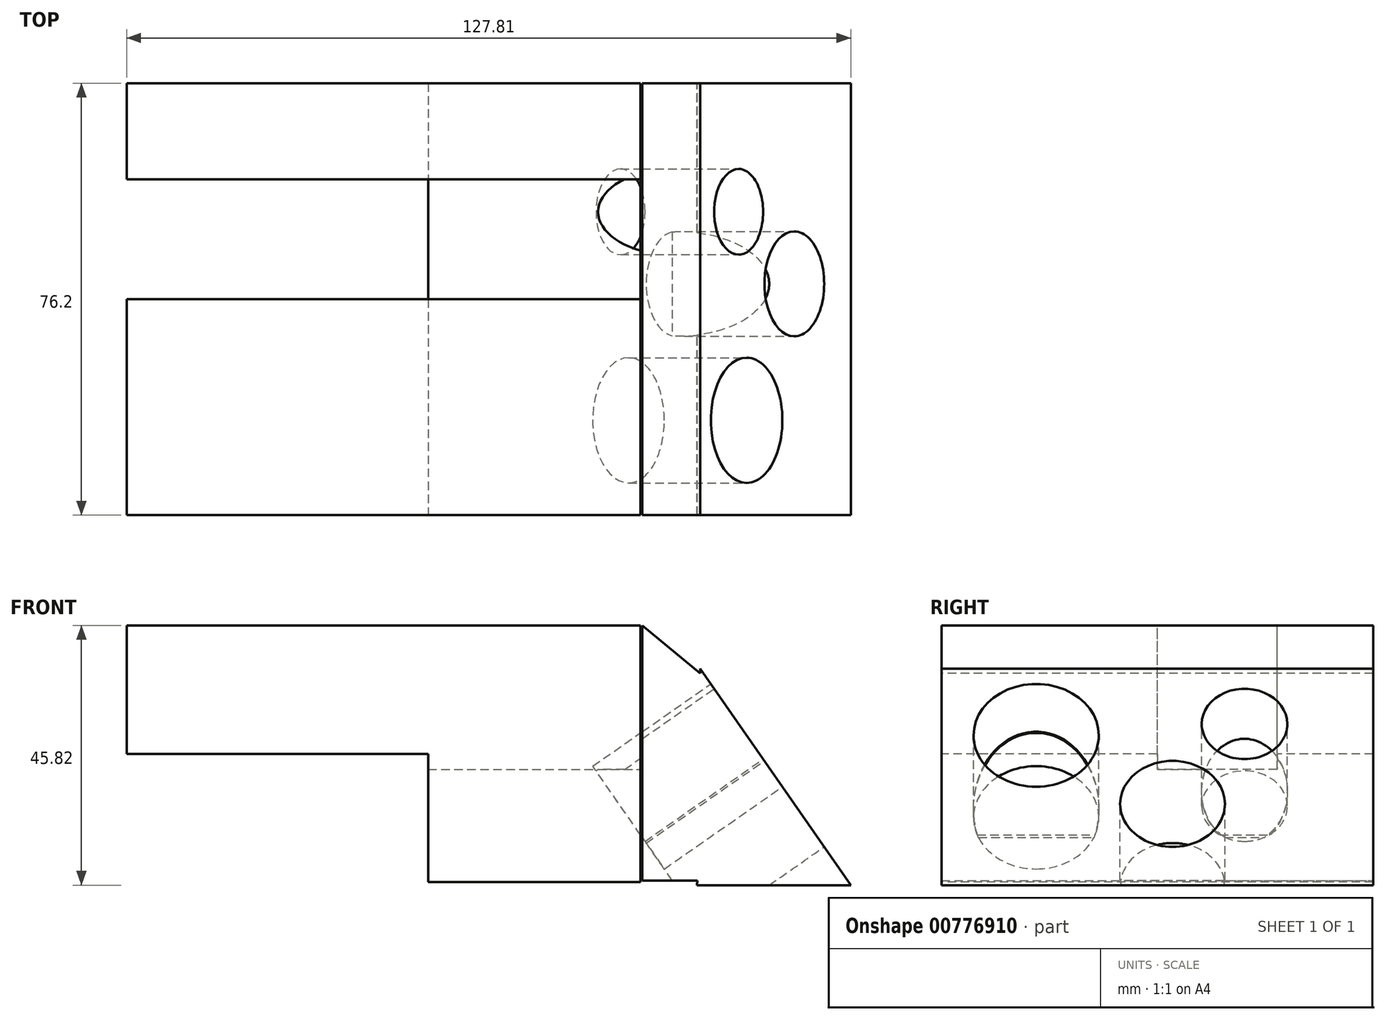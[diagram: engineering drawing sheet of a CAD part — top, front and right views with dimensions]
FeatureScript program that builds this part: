
annotation { "Feature Type Name" : "Feature", "Feature Type Description" : "" }
export const myFeature = defineFeature(function(context is Context, id is Id, definition is map)
    precondition{}
    {
        {
            var Q0;
            Q0=qCreatedBy(makeId("Front.planeOp"),FACE);
            var sketch = newSketch(context, id + "F0", { "sketchPlane" : qUnion([Q0])});
            skLineSegment(sketch, "E0.bottom", {"start": v(-53.2, -45.3) * mm, "end": v(37.5, -45.3) * mm});
            skLineSegment(sketch, "E0.top", {"start": v(-53.2, 0) * mm, "end": v(37.5, 0) * mm});
            skLineSegment(sketch, "E0.left", {"start": v(-53.2, -45.3) * mm, "end": v(-53.2, 0) * mm});
            skLineSegment(sketch, "E0.right", {"start": v(37.5, -45.3) * mm, "end": v(37.5, 0) * mm});
            skSolve(sketch);
        }
        {
            var Q0;
            Q0=makeQuery(id+"F0.imprint","IMPRINT",FACE,{"disambiguationData":[TD([[makeQuery(id+"F0.imprint","IMPRINT",EDGE,{"derivedFrom":sQuery(id+"F0.wireOp",EDGE,"E0.bottom")}),1.0]])]});
            extrude(context, id + "F1", {"entities" : qUnion([Q0]), "depth" : 76.2 * mm, "offsetDistance" : 25.4 * mm});
        }
        {
            var Q0;
            Q0=makeQuery(id+"F1.opExtrude","SWEPT_FACE",FACE,{"disambiguationData":[OSD([sQuery(id+"F0.wireOp",EDGE,"E0.top")])]});
            var sketch = newSketch(context, id + "F2", { "sketchPlane" : qUnion([Q0])});
            skLineSegment(sketch, "E1.bottom", {"start": v(-53.2, -38.1) * mm, "end": v(37.5, -38.1) * mm});
            skLineSegment(sketch, "E1.top", {"start": v(-53.2, -16.94) * mm, "end": v(37.5, -16.94) * mm});
            skLineSegment(sketch, "E1.left", {"start": v(-53.2, -38.1) * mm, "end": v(-53.2, -16.94) * mm});
            skLineSegment(sketch, "E1.right", {"start": v(37.5, -38.1) * mm, "end": v(37.5, -16.94) * mm});
            skSolve(sketch);
        }
        {
            var Q0;
            Q0=makeQuery(id+"F2.imprint","IMPRINT",FACE,{"disambiguationData":[TD([[makeQuery(id+"F2.imprint","IMPRINT",EDGE,{"derivedFrom":sQuery(id+"F2.wireOp",EDGE,"E1.bottom")}),1.0]])]});
            extrude(context, id + "F3", {"entities" : qUnion([Q0]), "operationType" : NewBodyOperationType.REMOVE, "oppositeDirection" : true, "depth" : 25.4 * mm, "offsetDistance" : 25.4 * mm});
        }
        {
            var Q0;
            Q0=qCreatedBy(makeId("Front.planeOp"),FACE);
            var sketch = newSketch(context, id + "F4", { "sketchPlane" : qUnion([Q0])});
            skLineSegment(sketch, "E2", {"start": v(37.8, -45) * mm, "end": v(37.8, 0) * mm});
            skLineSegment(sketch, "E3", {"start": v(37.8, 0) * mm, "end": v(48.03, -8.45) * mm});
            skLineSegment(sketch, "E4", {"start": v(48.03, -8.45) * mm, "end": v(48.03, -45) * mm});
            skLineSegment(sketch, "E5", {"start": v(48.03, -45) * mm, "end": v(37.8, -45) * mm});
            skSolve(sketch);
        }
        {
            var Q0;
            Q0=makeQuery(id+"F4.imprint","IMPRINT",FACE,{"disambiguationData":[TD([[makeQuery(id+"F4.imprint","IMPRINT",EDGE,{"derivedFrom":sQuery(id+"F4.wireOp",EDGE,"E2")}),-1.0]])]});
            extrude(context, id + "F5", {"entities" : qUnion([Q0]), "depth" : 76.2 * mm, "offsetDistance" : 25.4 * mm});
        }
        {
            var Q0;
            Q0=qCreatedBy(makeId("Front.planeOp"),FACE);
            var sketch = newSketch(context, id + "F6", { "sketchPlane" : qUnion([Q0])});
            skLineSegment(sketch, "E6", {"start": v(48.03, -7.62) * mm, "end": v(74.61, -45.82) * mm});
            skLineSegment(sketch, "E7", {"start": v(74.61, -45.82) * mm, "end": v(47.48, -45.82) * mm});
            skLineSegment(sketch, "E8", {"start": v(47.48, -45.82) * mm, "end": v(48.03, -7.62) * mm});
            skSolve(sketch);
        }
        {
            var Q0;
            Q0 = qSketchRegion(id + "F6", true);
            extrude(context, id + "F7", {"entities" : qUnion([Q0]), "operationType" : NewBodyOperationType.ADD, "depth" : 76.2 * mm, "offsetDistance" : 25.4 * mm});
        }
        {
            var Q0;
            Q0=makeQuery(id+"F1.opExtrude","CAP_FACE",FACE,{"disambiguationData":[OSD([sQuery(id+"F0.wireOp",EDGE,"E0.bottom"),sQuery(id+"F0.wireOp",EDGE,"E0.top"),sQuery(id+"F0.wireOp",EDGE,"E0.left"),sQuery(id+"F0.wireOp",EDGE,"E0.right")])],"isStart":false});
            var sketch = newSketch(context, id + "F8", { "sketchPlane" : qUnion([Q0])});
            skLineSegment(sketch, "E9.bottom", {"start": v(-53.2, -22.65) * mm, "end": v(0, -22.65) * mm});
            skLineSegment(sketch, "E9.top", {"start": v(-53.2, -45.3) * mm, "end": v(0, -45.3) * mm});
            skLineSegment(sketch, "E9.left", {"start": v(-53.2, -22.65) * mm, "end": v(-53.2, -45.3) * mm});
            skLineSegment(sketch, "E9.right", {"start": v(0, -22.65) * mm, "end": v(0, -45.3) * mm});
            skSolve(sketch);
        }
        {
            var Q0;
            Q0=makeQuery(id+"F8.imprint","IMPRINT",FACE,{"disambiguationData":[TD([[makeQuery(id+"F8.imprint","IMPRINT",EDGE,{"derivedFrom":sQuery(id+"F8.wireOp",EDGE,"E9.bottom")}),-1.0]])]});
            extrude(context, id + "F9", {"entities" : qUnion([Q0]), "operationType" : NewBodyOperationType.REMOVE, "oppositeDirection" : true, "depth" : 76.2 * mm, "offsetDistance" : 25.4 * mm});
        }
        {
            var Q0;
            Q0=makeQuery(id+"F7.opExtrude","SWEPT_FACE",FACE,{"disambiguationData":[OSD([sQuery(id+"F6.wireOp",EDGE,"E6")])]});
            var sketch = newSketch(context, id + "F10", { "sketchPlane" : qUnion([Q0])});
            skCircle(sketch, "E10", {"center": v(-59.48, -48.02) * mm, "radius": 11.05 * mm});
            skSolve(sketch);
        }
        {
            var Q0;
            Q0 = qSketchRegion(id + "F10", true);
            extrude(context, id + "F11", {"entities" : qUnion([Q0]), "operationType" : NewBodyOperationType.REMOVE, "oppositeDirection" : true, "depth" : 25.4 * mm, "offsetDistance" : 25.4 * mm});
        }
        {
            var Q0;
            Q0=makeQuery(id+"F7.opExtrude","SWEPT_FACE",FACE,{"disambiguationData":[OSD([sQuery(id+"F6.wireOp",EDGE,"E6")])]});
            var sketch = newSketch(context, id + "F12", { "sketchPlane" : qUnion([Q0])});
            skCircle(sketch, "E11", {"center": v(-22.7, -45.56) * mm, "radius": 7.57 * mm});
            skSolve(sketch);
        }
        {
            var Q0;
            Q0 = qSketchRegion(id + "F12", true);
            extrude(context, id + "F13", {"entities" : qUnion([Q0]), "operationType" : NewBodyOperationType.REMOVE, "oppositeDirection" : true, "depth" : 25.4 * mm, "offsetDistance" : 25.4 * mm});
        }
        {
            var Q0;
            Q0=makeQuery(id+"F7.opExtrude","SWEPT_FACE",FACE,{"disambiguationData":[OSD([sQuery(id+"F6.wireOp",EDGE,"E6")])]});
            var sketch = newSketch(context, id + "F14", { "sketchPlane" : qUnion([Q0])});
            skCircle(sketch, "E12", {"center": v(-35.4, -62.75) * mm, "radius": 9.25 * mm});
            skSolve(sketch);
        }
        {
            var Q0;
            Q0 = qSketchRegion(id + "F14", true);
            extrude(context, id + "F15", {"entities" : qUnion([Q0]), "operationType" : NewBodyOperationType.REMOVE, "oppositeDirection" : true, "depth" : 25.4 * mm, "offsetDistance" : 25.4 * mm});
        }
    });
